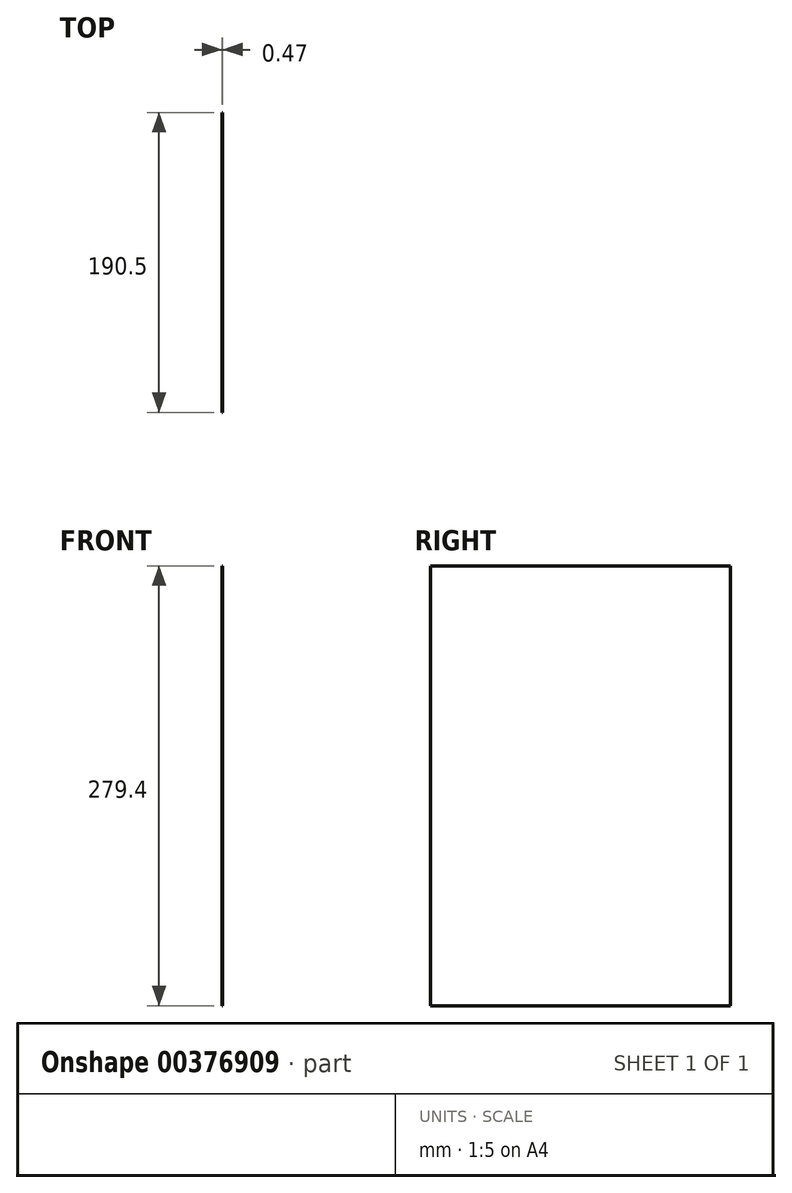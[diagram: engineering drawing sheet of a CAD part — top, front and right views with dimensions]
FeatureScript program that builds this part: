
annotation { "Feature Type Name" : "Feature", "Feature Type Description" : "" }
export const myFeature = defineFeature(function(context is Context, id is Id, definition is map)
    precondition{}
    {
        {
            var Q0;
            Q0=qCreatedBy(makeId("Right.planeOp"),FACE);
            var sketch = newSketch(context, id + "F0", { "sketchPlane" : qUnion([Q0])});
            skLineSegment(sketch, "E0.bottom", {"start": v(0, 0) * mm, "end": v(190.5, 0) * mm});
            skLineSegment(sketch, "E0.top", {"start": v(0, -279.4) * mm, "end": v(190.5, -279.4) * mm});
            skLineSegment(sketch, "E0.left", {"start": v(0, 0) * mm, "end": v(0, -279.4) * mm});
            skLineSegment(sketch, "E0.right", {"start": v(190.5, 0) * mm, "end": v(190.5, -279.4) * mm});
            skSolve(sketch);
        }
        {
            assignVariable(context, id + "F1", {"name" : "material", "anyValue" : 0.47});
        }
        {
            var Q0;
            Q0=makeQuery(id+"F0.imprint","IMPRINT",FACE,{"disambiguationData":[TD([[makeQuery(id+"F0.imprint","IMPRINT",EDGE,{"derivedFrom":sQuery(id+"F0.wireOp",EDGE,"E0.bottom")}),-1.0]])]});
            extrude(context, id + "F2", {"entities" : qUnion([Q0]), "depth" : (getVariable(context, 'material')) * mm});
        }
    });
